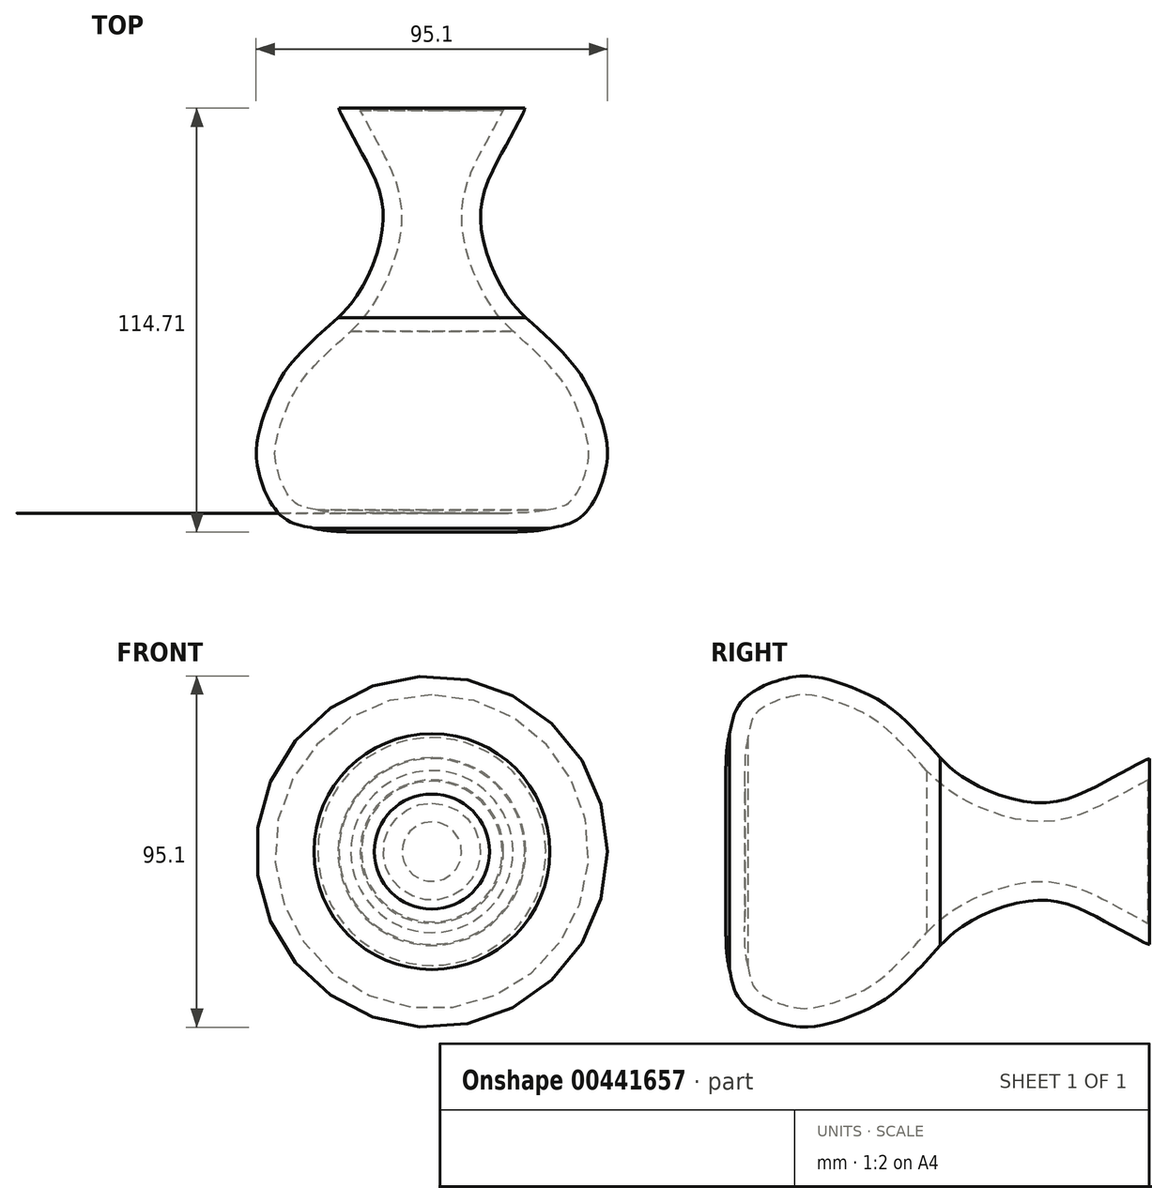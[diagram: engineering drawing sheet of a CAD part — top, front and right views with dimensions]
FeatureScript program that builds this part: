
annotation { "Feature Type Name" : "Feature", "Feature Type Description" : "" }
export const myFeature = defineFeature(function(context is Context, id is Id, definition is map)
    precondition{}
    {
        {
            var Q0;
            Q0=qCreatedBy(makeId("Top.planeOp"),FACE);
            var sketch = newSketch(context, id + "F0", { "sketchPlane" : qUnion([Q0])});
            skLineSegment(sketch, "E0", {"start": v(0, 56.65) * mm, "end": v(25.12, 56.65) * mm});
            skFitSpline(sketch, "E1", {"points": [v(25.4, 56.65) * mm, v(19.06, 44.84) * mm, v(13.16, 27.65) * mm, v(19.6, 6.98) * mm, v(25.4, 0) * mm], "startDerivative": vector(-25.73, -48.24) * mm, "endDerivative": vector(29.36, -28.8) * mm});
            skFitSpline(sketch, "E2", {"points": [v(25.4, 0) * mm, v(38.4, -12.9) * mm, v(44.57, -24.17) * mm, v(47.25, -40) * mm, v(40.81, -50.21) * mm, v(33.83, -56.39) * mm, v(15.57, -58) * mm], "startDerivative": vector(76.91, -69.24) * mm, "endDerivative": vector(-110.8, 1.9) * mm});
            skLineSegment(sketch, "E3", {"start": v(15.57, -58) * mm, "end": v(0, -58) * mm});
            skLineSegment(sketch, "E4", {"start": v(0, 56.65) * mm, "end": v(0, -58) * mm});
            skPoint(sketch, "E5.1.internal.orphan", {"position": v(47.25, -49.14) * mm});
            skFitSpline(sketch, "E6", {"points": [v(47.25, -40) * mm, v(45.44, -46.46) * mm, v(39.97, -54.31) * mm, v(31.93, -57.04) * mm], "startDerivative": vector(-4.3, -20.47) * mm, "endDerivative": vector(-25.31, -4.38) * mm});
            skLineSegment(sketch, "E7", {"start": v(25.28, 56.4) * mm, "end": v(25.12, 56.65) * mm});
            skSolve(sketch);
        }
        {
            var Q0;
            Q0 = qSketchRegion(id + "F0", true);
            var Q1;
            Q1=sQuery(id+"F0.wireOp",EDGE,"E4");
            revolve(context, id + "F1", {"entities" : qUnion([Q0]), "axis" : qUnion([Q1]), "revolveType" : RevolveType.FULL});
        }
        {
            var Q0;
            Q0=makeQuery(id+"F1.opRevolve","SWEPT_FACE",FACE,{"disambiguationData":[OSD([sQuery(id+"F0.wireOp",EDGE,"E0")])]});
            shell(context, id + "F2", {"entities" : qUnion([Q0]), "thickness" : 5.08 * mm});
        }
        {
            var Q0;
            Q0=makeQuery(id+"F1.opRevolve","SWEPT_EDGE",EDGE,{"disambiguationData":[OSD([sQuery(id+"F0.wireOp",EDGE,"E1"),sQuery(id+"F0.wireOp",EDGE,"E7")])]});
            fillet(context, id + "F3", {"entities" : qUnion([Q0]), "radius" : 5.08 * mm, "tangentPropagation" : true, "allowEdgeOverflow" : false});
        }
    });
